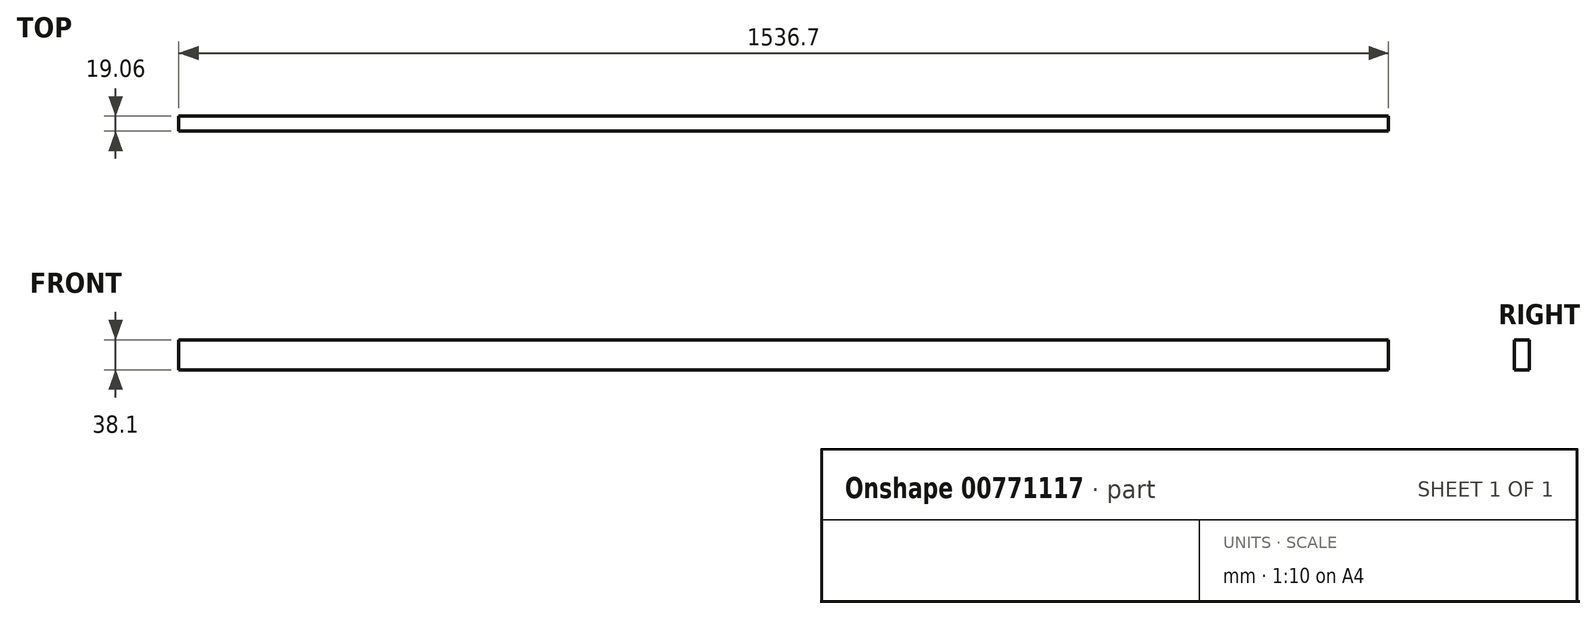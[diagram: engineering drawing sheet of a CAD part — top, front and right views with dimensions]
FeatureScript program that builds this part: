
annotation { "Feature Type Name" : "Feature", "Feature Type Description" : "" }
export const myFeature = defineFeature(function(context is Context, id is Id, definition is map)
    precondition{}
    {
        {
            var Q0;
            Q0=qCreatedBy(makeId("Right.planeOp"),FACE);
            var sketch = newSketch(context, id + "F0", { "sketchPlane" : qUnion([Q0])});
            skLineSegment(sketch, "E0.bottom", {"start": v(-9.52, 19.05) * mm, "end": v(9.53, 19.05) * mm});
            skLineSegment(sketch, "E0.top", {"start": v(-9.53, -19.05) * mm, "end": v(9.52, -19.05) * mm});
            skLineSegment(sketch, "E0.left", {"start": v(-9.52, 19.05) * mm, "end": v(-9.53, -19.05) * mm});
            skLineSegment(sketch, "E0.right", {"start": v(9.53, 19.05) * mm, "end": v(9.52, -19.05) * mm});
            skPoint(sketch, "E0.middle", {"position": v(0, 0) * mm});
            skSolve(sketch);
        }
        {
            var Q0;
            Q0=makeQuery(id+"F0.imprint","IMPRINT",FACE,{"disambiguationData":[TD([[makeQuery(id+"F0.imprint","IMPRINT",EDGE,{"derivedFrom":sQuery(id+"F0.wireOp",EDGE,"E0.bottom")}),-1.0]])]});
            extrude(context, id + "F1", {"entities" : qUnion([Q0]), "endBound" : BoundingType.SYMMETRIC, "depth" : 1536.7 * mm, "offsetDistance" : 25.4 * mm});
        }
    });
